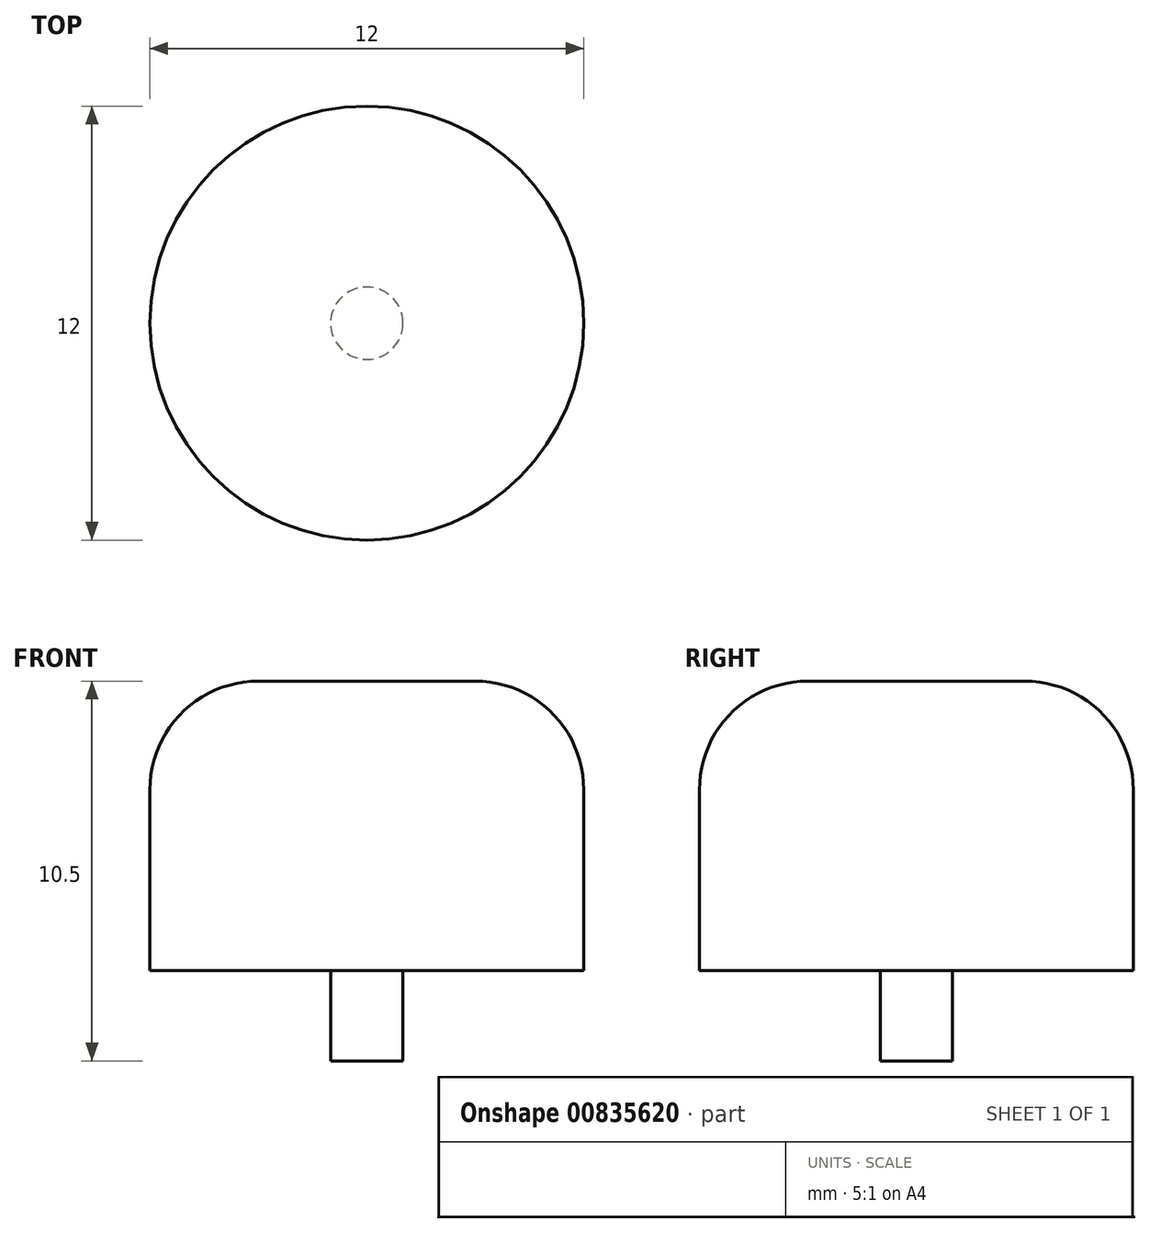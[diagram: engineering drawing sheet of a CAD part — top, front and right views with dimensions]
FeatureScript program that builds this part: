
annotation { "Feature Type Name" : "Feature", "Feature Type Description" : "" }
export const myFeature = defineFeature(function(context is Context, id is Id, definition is map)
    precondition{}
    {
        {
            var Q0;
            Q0=qCreatedBy(makeId("Front.planeOp"),FACE);
            var sketch = newSketch(context, id + "F0", { "sketchPlane" : qUnion([Q0])});
            skLineSegment(sketch, "E0", {"start": v(0, 0) * mm, "end": v(-1, 0) * mm});
            skLineSegment(sketch, "E1", {"start": v(-1, 0) * mm, "end": v(-1, 2.5) * mm});
            skLineSegment(sketch, "E2", {"start": v(-1, 2.5) * mm, "end": v(-6, 2.5) * mm});
            skLineSegment(sketch, "E3", {"start": v(-6, 2.5) * mm, "end": v(-6, 7.5) * mm});
            skLineSegment(sketch, "E4", {"start": v(-3, 10.5) * mm, "end": v(0, 10.5) * mm});
            skLineSegment(sketch, "E5", {"start": v(0, 10.5) * mm, "end": v(0, 0) * mm});
            skPoint(sketch, "E6.visualSharp", {"position": v(-6, 10.5) * mm});
            skArc(sketch, "E6.filletArc", {"start": v(-3, 10.5) * mm, "mid": v(-5.12, 9.62) * mm, "end": v(-6, 7.5) * mm});
            skPoint(sketch, "E7", {"position": v(0, 10.5) * mm});
            skSolve(sketch);
        }
        {
            var Q0;
            Q0=makeQuery(id+"F0.imprint","IMPRINT",FACE,{"disambiguationData":[TD([[makeQuery(id+"F0.imprint","IMPRINT",EDGE,{"derivedFrom":sQuery(id+"F0.wireOp",EDGE,"E0")}),-1.0]])]});
            var Q1;
            Q1=sQuery(id+"F0.wireOp",EDGE,"E5");
            revolve(context, id + "F1", {"surfaceOperationType" : NewSurfaceOperationType.NEW, "entities" : qUnion([Q0]), "axis" : qUnion([Q1]), "revolveType" : RevolveType.FULL});
        }
    });
